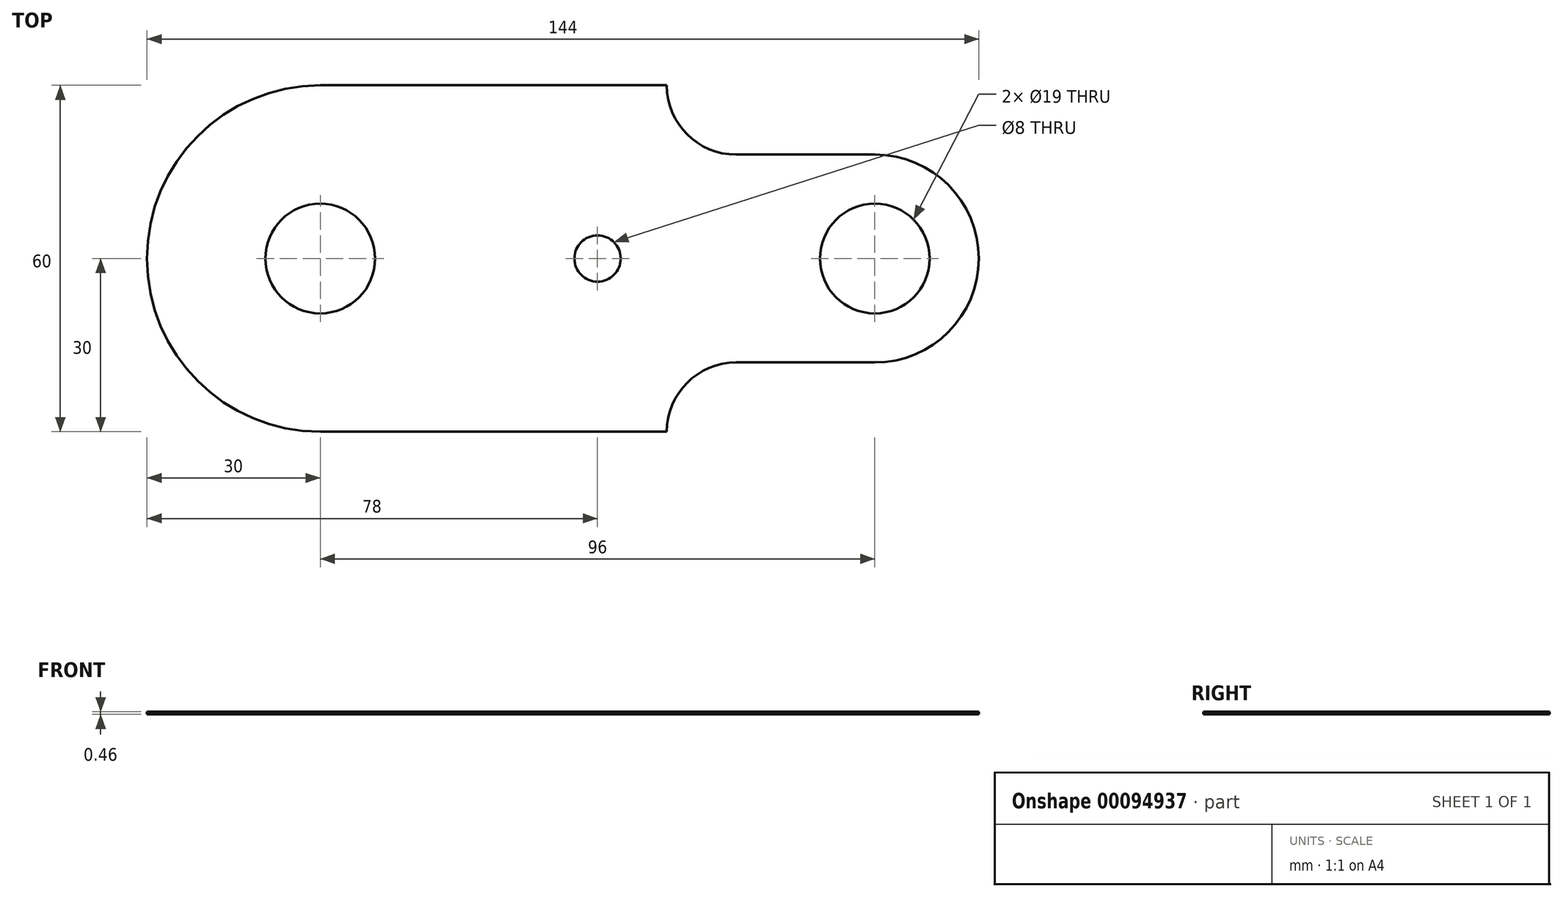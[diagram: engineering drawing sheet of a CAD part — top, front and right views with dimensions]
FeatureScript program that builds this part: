
annotation { "Feature Type Name" : "Feature", "Feature Type Description" : "" }
export const myFeature = defineFeature(function(context is Context, id is Id, definition is map)
    precondition{}
    {
        {
            var Q0;
            Q0=qCreatedBy(makeId("Front.planeOp"),FACE);
            var sketch = newSketch(context, id + "F0", { "sketchPlane" : qUnion([Q0])});
            skLineSegment(sketch, "E0", {"start": v(-25, 15) * mm, "end": v(-25, -20) * mm});
            skLineSegment(sketch, "E1", {"start": v(-25, -20) * mm, "end": v(25, -20) * mm});
            skLineSegment(sketch, "E2", {"start": v(-25, 15) * mm, "end": v(0, 15) * mm});
            skLineSegment(sketch, "E3", {"start": v(25, -20) * mm, "end": v(25, -5) * mm});
            skCircle(sketch, "E4", {"center": v(-5, 0) * mm, "radius": 5 * mm});
            skLineSegment(sketch, "E5", {"start": v(25, -5) * mm, "end": v(0, 15) * mm});
            skSolve(sketch);
        }
        {
            var Q0;
            Q0=qCreatedBy(makeId("Top.planeOp"),FACE);
            var sketch = newSketch(context, id + "F1", { "sketchPlane" : qUnion([Q0])});
            skCircle(sketch, "E6", {"center": v(0, 0) * mm, "radius": 9.5 * mm});
            skCircle(sketch, "E7", {"center": v(96, 0) * mm, "radius": 9.5 * mm});
            skCircle(sketch, "E8", {"center": v(48, 0) * mm, "radius": 4 * mm});
            skArc(sketch, "E9", {"start": v(0, 30) * mm, "mid": v(-21.21, 21.21) * mm, "end": v(-30, 0) * mm});
            skArc(sketch, "E10", {"start": v(0, -30) * mm, "mid": v(-21.21, -21.21) * mm, "end": v(-30, 0) * mm});
            skLineSegment(sketch, "E11", {"start": v(96, 18) * mm, "end": v(72, 18) * mm});
            skLineSegment(sketch, "E12", {"start": v(96, -18) * mm, "end": v(72, -18) * mm});
            skArc(sketch, "E13", {"start": v(96, 18) * mm, "mid": v(108.73, 12.73) * mm, "end": v(114, 0) * mm});
            skArc(sketch, "E14", {"start": v(96, -18) * mm, "mid": v(108.73, -12.73) * mm, "end": v(114, 0) * mm});
            skLineSegment(sketch, "E15", {"start": v(0, -30) * mm, "end": v(60, -30) * mm});
            skArc(sketch, "E16", {"start": v(72, 18) * mm, "mid": v(63.51, 21.51) * mm, "end": v(60, 30) * mm});
            skArc(sketch, "E17", {"start": v(72, -18) * mm, "mid": v(63.51, -21.51) * mm, "end": v(60, -30) * mm});
            skLineSegment(sketch, "E18", {"start": v(0, 30) * mm, "end": v(60, 30) * mm});
            skSolve(sketch);
        }
        {
            var Q0;
            Q0=makeQuery(id+"F1.imprint","IMPRINT",FACE,{"disambiguationData":[TD([[makeQuery(id+"F1.imprint","IMPRINT",EDGE,{"derivedFrom":sQuery(id+"F1.wireOp",EDGE,"E6")}),-1.0]])]});
            extrude(context, id + "F2", {"entities" : qUnion([Q0]), "depth" : 0.46 * mm});
        }
    });
